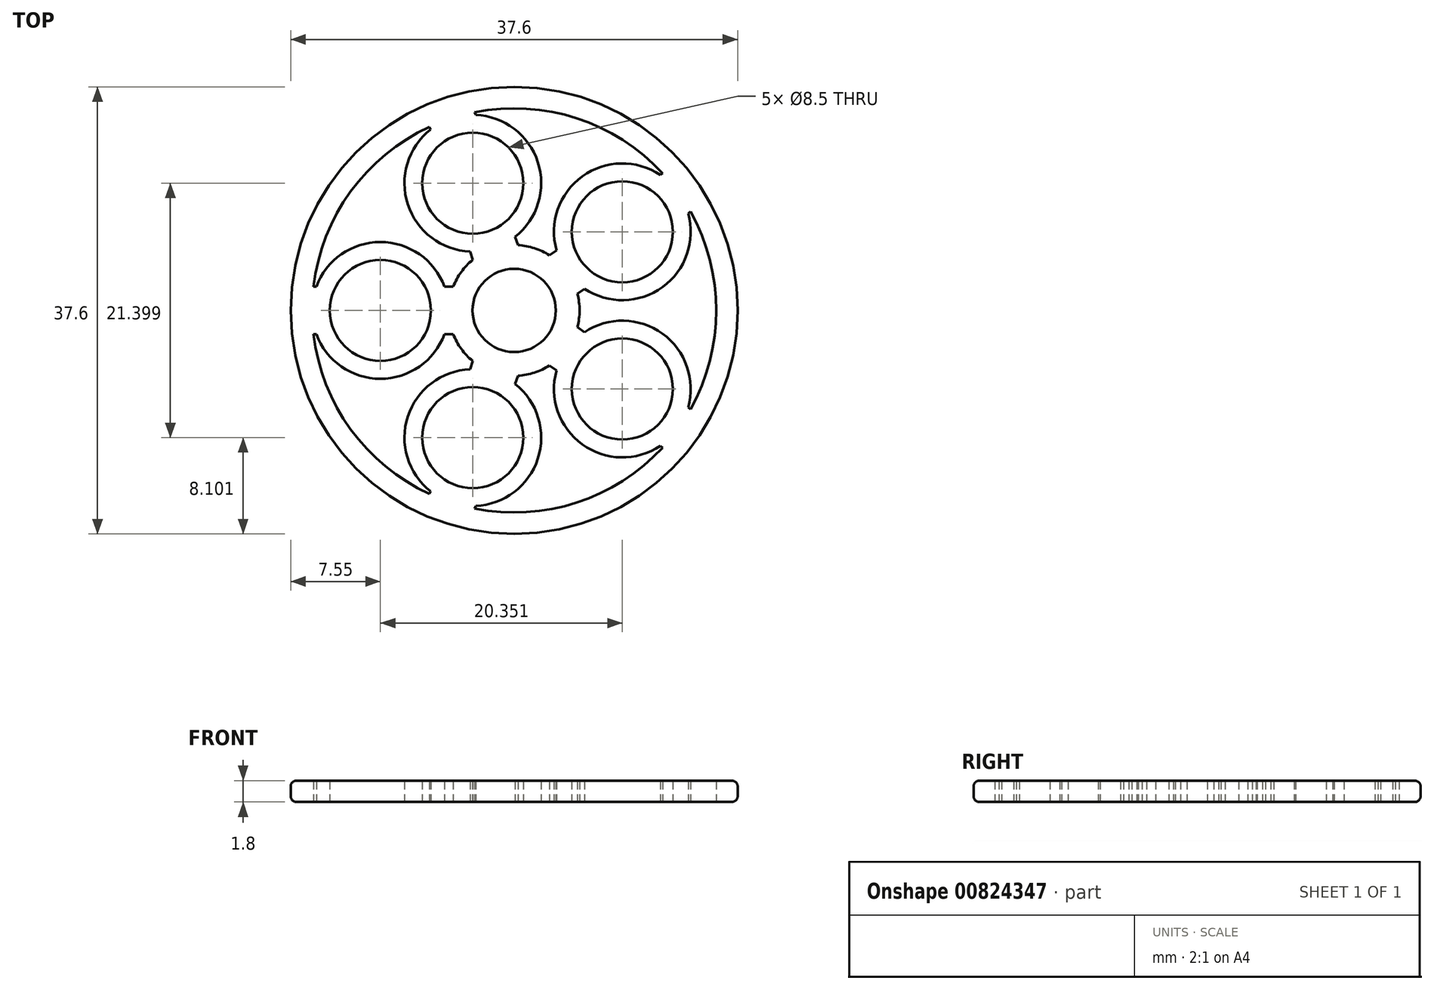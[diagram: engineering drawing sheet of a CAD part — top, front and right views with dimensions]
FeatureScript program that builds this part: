
annotation { "Feature Type Name" : "Feature", "Feature Type Description" : "" }
export const myFeature = defineFeature(function(context is Context, id is Id, definition is map)
    precondition{}
    {
        {
            var Q0;
            Q0=qCreatedBy(makeId("Top.planeOp"),FACE);
            var sketch = newSketch(context, id + "F0", { "sketchPlane" : qUnion([Q0])});
            skCircle(sketch, "E0", {"center": v(0, 0) * mm, "radius": 18.8 * mm});
            skCircle(sketch, "E1", {"center": v(0, 0) * mm, "radius": 3.5 * mm});
            skArc(sketch, "E2", {"start": v(-3.49, 4.25) * mm, "mid": v(-4.45, 3.23) * mm, "end": v(-5.12, 2) * mm});
            skArc(sketch, "E3", {"start": v(-7.12, 15.44) * mm, "mid": v(-13.75, 10) * mm, "end": v(-16.88, 2) * mm});
            skArc(sketch, "E4", {"start": v(-5.86, 2) * mm, "mid": v(-11.25, 5.75) * mm, "end": v(-16.64, 2) * mm});
            skPoint(sketch, "E5.orphan", {"position": v(-17, 0) * mm});
            skPoint(sketch, "E6.end.orphan", {"position": v(-5.5, 0) * mm});
            skCircle(sketch, "E7", {"center": v(-11.25, 0) * mm, "radius": 4.25 * mm});
            skArc(sketch, "E8.1.0", {"start": v(-3.71, -4.95) * mm, "mid": v(-8.95, -8.92) * mm, "end": v(-7.04, -15.2) * mm});
            skCircle(sketch, "E8.1.1", {"center": v(-3.48, -10.7) * mm, "radius": 4.25 * mm});
            skArc(sketch, "E8.2.0", {"start": v(14.64, -8.16) * mm, "mid": v(12.48, -1.96) * mm, "end": v(5.92, -1.83) * mm});
            skCircle(sketch, "E8.2.1", {"center": v(9.1, -6.61) * mm, "radius": 4.25 * mm});
            skArc(sketch, "E9.1.3.0", {"start": v(5.92, 1.83) * mm, "mid": v(12.48, 1.96) * mm, "end": v(14.64, 8.16) * mm});
            skCircle(sketch, "E9.2.3.0", {"center": v(9.1, 6.61) * mm, "radius": 4.25 * mm});
            skArc(sketch, "E9.1.4.0", {"start": v(-7.04, 15.2) * mm, "mid": v(-8.95, 8.92) * mm, "end": v(-3.71, 4.95) * mm});
            skCircle(sketch, "E9.2.4.0", {"center": v(-3.48, 10.7) * mm, "radius": 4.25 * mm});
            skLineSegment(sketch, "E10", {"start": v(0, 0) * mm, "end": v(0, 2) * mm});
            skLineSegment(sketch, "E11", {"start": v(-5.12, 2) * mm, "end": v(-5.86, 2) * mm});
            skLineSegment(sketch, "E12", {"start": v(-16.88, -2) * mm, "end": v(-16.64, -2) * mm});
            skPoint(sketch, "E13.orphan", {"position": v(0, -2) * mm});
            skLineSegment(sketch, "E14.1.0", {"start": v(-3.49, -4.25) * mm, "end": v(-3.71, -4.95) * mm});
            skLineSegment(sketch, "E14.1.1", {"start": v(-3.31, -16.67) * mm, "end": v(-3.24, -16.44) * mm});
            skLineSegment(sketch, "E14.2.0", {"start": v(2.97, -4.63) * mm, "end": v(3.56, -5.06) * mm});
            skLineSegment(sketch, "E14.2.1", {"start": v(14.83, -8.3) * mm, "end": v(14.64, -8.16) * mm});
            skLineSegment(sketch, "E15.2.3.0", {"start": v(5.32, 1.4) * mm, "end": v(5.92, 1.83) * mm});
            skLineSegment(sketch, "E15.3.3.0", {"start": v(12.48, 11.54) * mm, "end": v(12.29, 11.4) * mm});
            skLineSegment(sketch, "E15.2.4.0", {"start": v(0.32, 5.5) * mm, "end": v(0.1, 6.2) * mm});
            skLineSegment(sketch, "E15.3.4.0", {"start": v(-7.12, 15.44) * mm, "end": v(-7.04, 15.2) * mm});
            skLineSegment(sketch, "E16.trimOffspring", {"start": v(-3.71, 4.95) * mm, "end": v(-3.49, 4.25) * mm});
            skLineSegment(sketch, "E17.trimOffspring", {"start": v(-3.24, 16.44) * mm, "end": v(-3.31, 16.67) * mm});
            skArc(sketch, "E18.trimOffspring", {"start": v(0.1, 6.2) * mm, "mid": v(2, 12.48) * mm, "end": v(-3.24, 16.44) * mm});
            skPoint(sketch, "E19.orphan", {"position": v(-2.79, 2.11) * mm});
            skPoint(sketch, "E20.orphan", {"position": v(1.01, 3.35) * mm});
            skPoint(sketch, "E21.orphan", {"position": v(1.15, 3.3) * mm});
            skPoint(sketch, "E22.orphan", {"position": v(3.5, 0.07) * mm});
            skArc(sketch, "E23.trimOffspring", {"start": v(2.97, 4.63) * mm, "mid": v(1.7, 5.23) * mm, "end": v(0.32, 5.5) * mm});
            skLineSegment(sketch, "E24.trimOffspring", {"start": v(3.56, 5.06) * mm, "end": v(2.97, 4.63) * mm});
            skLineSegment(sketch, "E25.trimOffspring", {"start": v(14.64, 8.16) * mm, "end": v(14.83, 8.3) * mm});
            skArc(sketch, "E26.trimOffspring", {"start": v(12.29, 11.4) * mm, "mid": v(5.72, 11.26) * mm, "end": v(3.56, 5.06) * mm});
            skArc(sketch, "E27.trimOffspring", {"start": v(12.48, 11.54) * mm, "mid": v(5.25, 16.17) * mm, "end": v(-3.31, 16.67) * mm});
            skLineSegment(sketch, "E28.trimOffspring", {"start": v(-16.64, 2) * mm, "end": v(-16.88, 2) * mm});
            skLineSegment(sketch, "E29.trimOffspring", {"start": v(-5.86, -2) * mm, "end": v(-5.12, -2) * mm});
            skPoint(sketch, "E30.orphan", {"position": v(-2.87, -2) * mm});
            skPoint(sketch, "E31.orphan", {"position": v(-2.87, 2) * mm});
            skArc(sketch, "E32.trimOffspring", {"start": v(-5.12, -2) * mm, "mid": v(-4.45, -3.23) * mm, "end": v(-3.49, -4.25) * mm});
            skArc(sketch, "E33.trimOffspring", {"start": v(-16.64, -2) * mm, "mid": v(-11.25, -5.75) * mm, "end": v(-5.86, -2) * mm});
            skArc(sketch, "E34.trimOffspring", {"start": v(-16.88, -2) * mm, "mid": v(-13.75, -10) * mm, "end": v(-7.12, -15.44) * mm});
            skPoint(sketch, "E35.orphan", {"position": v(3.5, -0.07) * mm});
            skPoint(sketch, "E36.orphan", {"position": v(1.15, -3.3) * mm});
            skPoint(sketch, "E37.orphan", {"position": v(1.01, -3.35) * mm});
            skPoint(sketch, "E38.orphan", {"position": v(-2.79, -2.11) * mm});
            skLineSegment(sketch, "E39.trimOffspring", {"start": v(5.92, -1.83) * mm, "end": v(5.32, -1.4) * mm});
            skLineSegment(sketch, "E40.trimOffspring", {"start": v(12.29, -11.4) * mm, "end": v(12.48, -11.54) * mm});
            skArc(sketch, "E41.trimOffspring", {"start": v(14.83, -8.3) * mm, "mid": v(17, 0) * mm, "end": v(14.83, 8.3) * mm});
            skArc(sketch, "E42.trimOffspring", {"start": v(3.56, -5.06) * mm, "mid": v(5.72, -11.26) * mm, "end": v(12.29, -11.4) * mm});
            skArc(sketch, "E43.trimOffspring", {"start": v(5.32, -1.4) * mm, "mid": v(5.5, 0) * mm, "end": v(5.32, 1.4) * mm});
            skArc(sketch, "E44.trimOffspring", {"start": v(0.32, -5.5) * mm, "mid": v(1.7, -5.23) * mm, "end": v(2.97, -4.63) * mm});
            skLineSegment(sketch, "E45.trimOffspring", {"start": v(0.1, -6.2) * mm, "end": v(0.32, -5.5) * mm});
            skLineSegment(sketch, "E46.trimOffspring", {"start": v(-7.04, -15.2) * mm, "end": v(-7.12, -15.44) * mm});
            skArc(sketch, "E47.trimOffspring", {"start": v(-3.24, -16.44) * mm, "mid": v(2, -12.48) * mm, "end": v(0.1, -6.2) * mm});
            skArc(sketch, "E48.trimOffspring", {"start": v(-3.31, -16.67) * mm, "mid": v(5.25, -16.17) * mm, "end": v(12.48, -11.54) * mm});
            skSolve(sketch);
        }
        {
            var Q0;
            Q0=makeQuery(id+"F0.imprint","IMPRINT",FACE,{"disambiguationData":[TD([[makeQuery(id+"F0.imprint","IMPRINT",EDGE,{"derivedFrom":sQuery(id+"F0.wireOp",EDGE,"E0")}),1.0]])]});
            extrude(context, id + "F1", {"entities" : qUnion([Q0]), "depth" : 1.8 * mm, "offsetDistance" : 25 * mm});
        }
        {
            var Q0;
            Q0=makeQuery(id+"F1.opExtrude","CAP_EDGE",EDGE,{"disambiguationData":[OSD([sQuery(id+"F0.wireOp",EDGE,"E0")])],"isStart":false});
            var Q1;
            Q1=makeQuery(id+"F1.opExtrude","CAP_EDGE",EDGE,{"disambiguationData":[OSD([sQuery(id+"F0.wireOp",EDGE,"E0")])],"isStart":true});
            fillet(context, id + "F2", {"entities" : qUnion([Q0, Q1]), "radius" : .5 * mm, "tangentPropagation" : true, "allowEdgeOverflow" : false});
        }
    });
